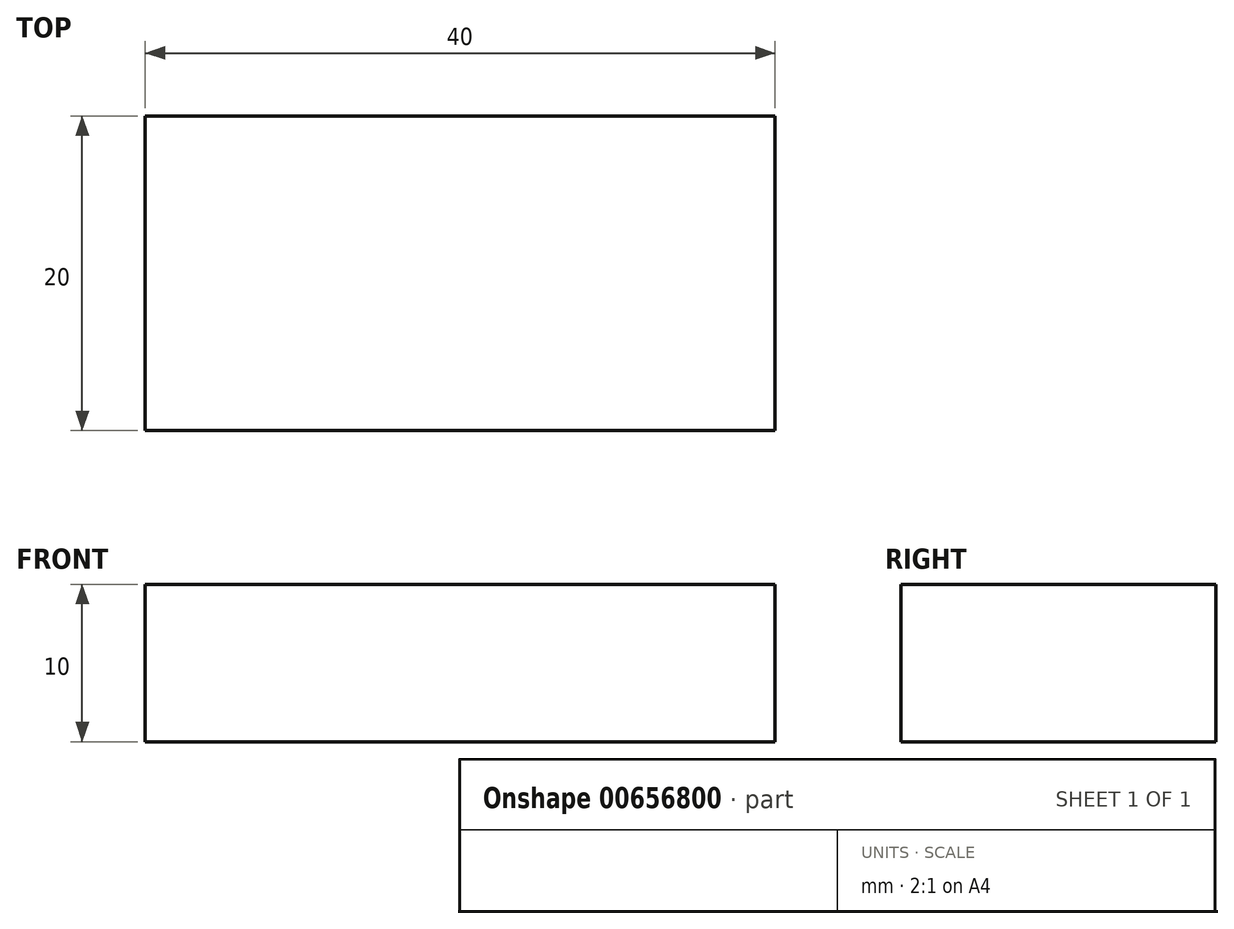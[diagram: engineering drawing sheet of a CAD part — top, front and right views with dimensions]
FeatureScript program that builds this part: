
annotation { "Feature Type Name" : "Feature", "Feature Type Description" : "" }
export const myFeature = defineFeature(function(context is Context, id is Id, definition is map)
    precondition{}
    {
        {
            var Q0;
            Q0=qCreatedBy(makeId("Top.planeOp"),FACE);
            var sketch = newSketch(context, id + "F0", { "sketchPlane" : qUnion([Q0])});
            skLineSegment(sketch, "E0.bottom", {"start": v(-38.21, 30.86) * mm, "end": v(1.79, 30.86) * mm});
            skLineSegment(sketch, "E0.top", {"start": v(-38.21, 10.86) * mm, "end": v(1.79, 10.86) * mm});
            skLineSegment(sketch, "E0.left", {"start": v(-38.21, 30.86) * mm, "end": v(-38.21, 10.86) * mm});
            skLineSegment(sketch, "E0.right", {"start": v(1.79, 30.86) * mm, "end": v(1.79, 10.86) * mm});
            skSolve(sketch);
        }
        {
            var Q0;
            Q0=makeQuery(id+"F0.imprint","IMPRINT",FACE,{"disambiguationData":[TD([[makeQuery(id+"F0.imprint","IMPRINT",EDGE,{"derivedFrom":sQuery(id+"F0.wireOp",EDGE,"E0.bottom")}),-1.0]])]});
            extrude(context, id + "F1", {"entities" : qUnion([Q0]), "depth" : 10 * mm, "offsetDistance" : 25 * mm});
        }
    });
